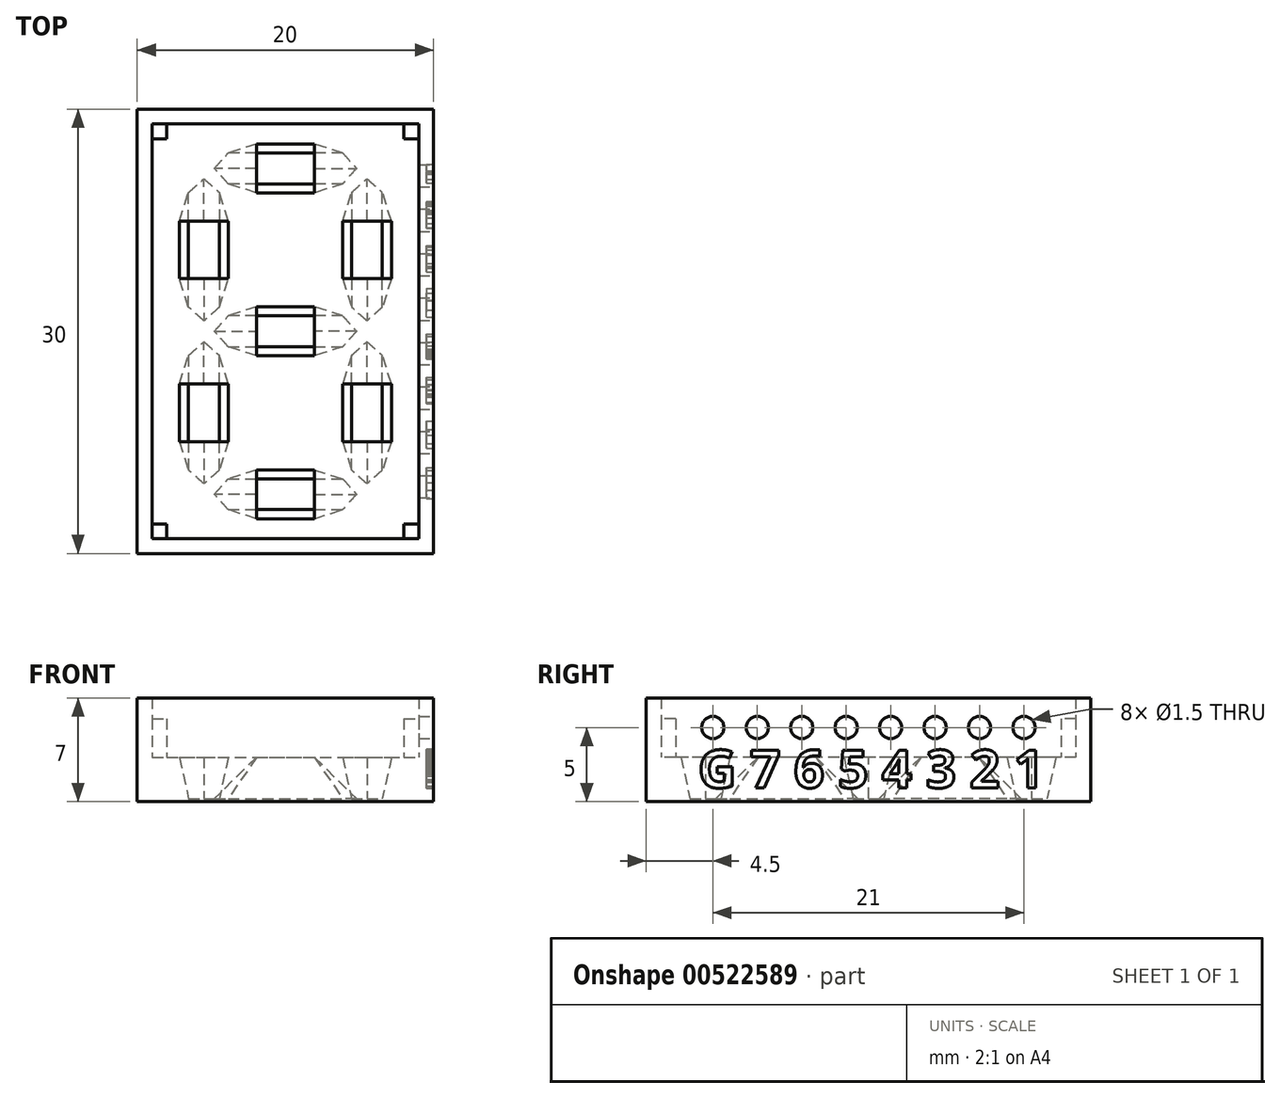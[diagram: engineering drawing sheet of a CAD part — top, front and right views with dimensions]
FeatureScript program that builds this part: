
annotation { "Feature Type Name" : "Feature", "Feature Type Description" : "" }
export const myFeature = defineFeature(function(context is Context, id is Id, definition is map)
    precondition{}
    {
        {
            var Q0;
            Q0=qCreatedBy(makeId("Top.planeOp"),FACE);
            cPlane(context, id + "F0", {"entities" : qUnion([Q0]), "cplaneType" : CPlaneType.OFFSET, "offset" : 3 * mm, "width" : 150 * mm, "height" : 150 * mm});
        }
        {
            var Q0;
            Q0=qCreatedBy(makeId("Top.planeOp"),FACE);
            var sketch = newSketch(context, id + "F1", { "sketchPlane" : qUnion([Q0])});
            skLineSegment(sketch, "E0.bottom", {"start": v(10, -15) * mm, "end": v(-10, -15) * mm});
            skLineSegment(sketch, "E0.top", {"start": v(10, 15) * mm, "end": v(-10, 15) * mm});
            skLineSegment(sketch, "E0.left", {"start": v(10, -15) * mm, "end": v(10, 15) * mm});
            skLineSegment(sketch, "E0.right", {"start": v(-10, -15) * mm, "end": v(-10, 15) * mm});
            skPoint(sketch, "E0.middle", {"position": v(0, 0) * mm});
            skLineSegment(sketch, "E1.bottom", {"start": v(4, -12) * mm, "end": v(-4, -12) * mm});
            skLineSegment(sketch, "E1.top", {"start": v(4, -10) * mm, "end": v(-4, -10) * mm});
            skPoint(sketch, "E1.middle", {"position": v(0, -11) * mm});
            skPoint(sketch, "E2", {"position": v(-5, -11) * mm});
            skPoint(sketch, "E3", {"position": v(5, -11) * mm});
            skPoint(sketch, "E4", {"position": v(4, -10) * mm});
            skPoint(sketch, "E5", {"position": v(-4, -10) * mm});
            skPoint(sketch, "E6", {"position": v(-4, -12) * mm});
            skPoint(sketch, "E7", {"position": v(4, -12) * mm});
            skLineSegment(sketch, "E8", {"start": v(-5, -11) * mm, "end": v(-4, -10) * mm});
            skLineSegment(sketch, "E9", {"start": v(-5, -11) * mm, "end": v(-4, -12) * mm});
            skLineSegment(sketch, "E10", {"start": v(4, -10) * mm, "end": v(5, -11) * mm});
            skLineSegment(sketch, "E11", {"start": v(4, -12) * mm, "end": v(5, -11) * mm});
            skLineSegment(sketch, "E12.bottom", {"start": v(4, -1) * mm, "end": v(-4, -1) * mm});
            skLineSegment(sketch, "E12.top", {"start": v(4, 1) * mm, "end": v(-4, 1) * mm});
            skPoint(sketch, "E13", {"position": v(-5, 0) * mm});
            skPoint(sketch, "E14", {"position": v(5, 0) * mm});
            skPoint(sketch, "E15", {"position": v(4, 1) * mm});
            skPoint(sketch, "E16", {"position": v(-4, 1) * mm});
            skPoint(sketch, "E17", {"position": v(-4, -1) * mm});
            skPoint(sketch, "E18", {"position": v(4, -1) * mm});
            skLineSegment(sketch, "E19", {"start": v(-5, 0) * mm, "end": v(-4, 1) * mm});
            skLineSegment(sketch, "E20", {"start": v(-5, 0) * mm, "end": v(-4, -1) * mm});
            skLineSegment(sketch, "E21", {"start": v(4, 1) * mm, "end": v(5, 0) * mm});
            skLineSegment(sketch, "E22", {"start": v(4, -1) * mm, "end": v(5, 0) * mm});
            skLineSegment(sketch, "E23.bottom", {"start": v(4, 10) * mm, "end": v(-4, 10) * mm});
            skLineSegment(sketch, "E23.top", {"start": v(4, 12) * mm, "end": v(-4, 12) * mm});
            skPoint(sketch, "E23.middle", {"position": v(0, 11) * mm});
            skPoint(sketch, "E24", {"position": v(-5, 11) * mm});
            skPoint(sketch, "E25", {"position": v(5, 11) * mm});
            skPoint(sketch, "E26", {"position": v(4, 12) * mm});
            skPoint(sketch, "E27", {"position": v(-4, 12) * mm});
            skPoint(sketch, "E28", {"position": v(-4, 10) * mm});
            skPoint(sketch, "E29", {"position": v(4, 10) * mm});
            skLineSegment(sketch, "E30", {"start": v(-5, 11) * mm, "end": v(-4, 12) * mm});
            skLineSegment(sketch, "E31", {"start": v(-5, 11) * mm, "end": v(-4, 10) * mm});
            skLineSegment(sketch, "E32", {"start": v(4, 12) * mm, "end": v(5, 11) * mm});
            skLineSegment(sketch, "E33", {"start": v(4, 10) * mm, "end": v(5, 11) * mm});
            skLineSegment(sketch, "E34.bottom", {"start": v(4.5, 1.5) * mm, "end": v(4.5, 9.5) * mm});
            skLineSegment(sketch, "E34.top", {"start": v(6.5, 1.5) * mm, "end": v(6.5, 9.5) * mm});
            skPoint(sketch, "E34.middle", {"position": v(5.5, 5.5) * mm});
            skPoint(sketch, "E35", {"position": v(5.5, 10.5) * mm});
            skPoint(sketch, "E36", {"position": v(5.5, 0.5) * mm});
            skPoint(sketch, "E37", {"position": v(6.5, 1.5) * mm});
            skPoint(sketch, "E38", {"position": v(6.5, 9.5) * mm});
            skPoint(sketch, "E39", {"position": v(4.5, 9.5) * mm});
            skPoint(sketch, "E40", {"position": v(4.5, 1.5) * mm});
            skLineSegment(sketch, "E41", {"start": v(5.5, 10.5) * mm, "end": v(6.5, 9.5) * mm});
            skLineSegment(sketch, "E42", {"start": v(5.5, 10.5) * mm, "end": v(4.5, 9.5) * mm});
            skLineSegment(sketch, "E43", {"start": v(6.5, 1.5) * mm, "end": v(5.5, 0.5) * mm});
            skLineSegment(sketch, "E44", {"start": v(4.5, 1.5) * mm, "end": v(5.5, 0.5) * mm});
            skLineSegment(sketch, "E45.bottom", {"start": v(4.5, -9.5) * mm, "end": v(4.5, -1.5) * mm});
            skLineSegment(sketch, "E45.top", {"start": v(6.5, -9.5) * mm, "end": v(6.5, -1.5) * mm});
            skPoint(sketch, "E45.middle", {"position": v(5.5, -5.5) * mm});
            skPoint(sketch, "E46", {"position": v(5.5, -0.5) * mm});
            skPoint(sketch, "E47", {"position": v(5.5, -10.5) * mm});
            skPoint(sketch, "E48", {"position": v(6.5, -9.5) * mm});
            skPoint(sketch, "E49", {"position": v(6.5, -1.5) * mm});
            skPoint(sketch, "E50", {"position": v(4.5, -1.5) * mm});
            skPoint(sketch, "E51", {"position": v(4.5, -9.5) * mm});
            skLineSegment(sketch, "E52", {"start": v(5.5, -0.5) * mm, "end": v(6.5, -1.5) * mm});
            skLineSegment(sketch, "E53", {"start": v(5.5, -0.5) * mm, "end": v(4.5, -1.5) * mm});
            skLineSegment(sketch, "E54", {"start": v(6.5, -9.5) * mm, "end": v(5.5, -10.5) * mm});
            skLineSegment(sketch, "E55", {"start": v(4.5, -9.5) * mm, "end": v(5.5, -10.5) * mm});
            skLineSegment(sketch, "E56.bottom", {"start": v(-6.5, 1.5) * mm, "end": v(-6.5, 9.5) * mm});
            skLineSegment(sketch, "E56.top", {"start": v(-4.5, 1.5) * mm, "end": v(-4.5, 9.5) * mm});
            skPoint(sketch, "E56.middle", {"position": v(-5.5, 5.5) * mm});
            skPoint(sketch, "E57", {"position": v(-5.5, 10.5) * mm});
            skPoint(sketch, "E58", {"position": v(-5.5, 0.5) * mm});
            skPoint(sketch, "E59", {"position": v(-4.5, 1.5) * mm});
            skPoint(sketch, "E60", {"position": v(-4.5, 9.5) * mm});
            skPoint(sketch, "E61", {"position": v(-6.5, 9.5) * mm});
            skPoint(sketch, "E62", {"position": v(-6.5, 1.5) * mm});
            skLineSegment(sketch, "E63", {"start": v(-5.5, 10.5) * mm, "end": v(-4.5, 9.5) * mm});
            skLineSegment(sketch, "E64", {"start": v(-5.5, 10.5) * mm, "end": v(-6.5, 9.5) * mm});
            skLineSegment(sketch, "E65", {"start": v(-4.5, 1.5) * mm, "end": v(-5.5, 0.5) * mm});
            skLineSegment(sketch, "E66", {"start": v(-6.5, 1.5) * mm, "end": v(-5.5, 0.5) * mm});
            skLineSegment(sketch, "E67.bottom", {"start": v(-6.5, -9.5) * mm, "end": v(-6.5, -1.5) * mm});
            skLineSegment(sketch, "E67.top", {"start": v(-4.5, -9.5) * mm, "end": v(-4.5, -1.5) * mm});
            skPoint(sketch, "E67.middle", {"position": v(-5.5, -5.5) * mm});
            skPoint(sketch, "E68", {"position": v(-5.5, -0.5) * mm});
            skPoint(sketch, "E69", {"position": v(-5.5, -10.5) * mm});
            skPoint(sketch, "E70", {"position": v(-4.5, -9.5) * mm});
            skPoint(sketch, "E71", {"position": v(-4.5, -1.5) * mm});
            skPoint(sketch, "E72", {"position": v(-6.5, -1.5) * mm});
            skPoint(sketch, "E73", {"position": v(-6.5, -9.5) * mm});
            skLineSegment(sketch, "E74", {"start": v(-5.5, -0.5) * mm, "end": v(-4.5, -1.5) * mm});
            skLineSegment(sketch, "E75", {"start": v(-5.5, -0.5) * mm, "end": v(-6.5, -1.5) * mm});
            skLineSegment(sketch, "E76", {"start": v(-4.5, -9.5) * mm, "end": v(-5.5, -10.5) * mm});
            skLineSegment(sketch, "E77", {"start": v(-6.5, -9.5) * mm, "end": v(-5.5, -10.5) * mm});
            skLineSegment(sketch, "E78", {"start": v(0, 0) * mm, "end": v(0, 11) * mm, "construction": true});
            skLineSegment(sketch, "E79", {"start": v(0, 0) * mm, "end": v(0, -11) * mm, "construction": true});
            skLineSegment(sketch, "E80", {"start": v(0, 5.5) * mm, "end": v(5.5, 5.5) * mm, "construction": true});
            skLineSegment(sketch, "E81", {"start": v(5.5, 0) * mm, "end": v(5.5, -5.5) * mm, "construction": true});
            skLineSegment(sketch, "E82", {"start": v(0, -5.5) * mm, "end": v(-5.5, -5.5) * mm, "construction": true});
            skLineSegment(sketch, "E83", {"start": v(0, -5.5) * mm, "end": v(5.5, -5.5) * mm, "construction": true});
            skLineSegment(sketch, "E84", {"start": v(5.5, 0) * mm, "end": v(5.5, 5.5) * mm, "construction": true});
            skLineSegment(sketch, "E85", {"start": v(0, 5.5) * mm, "end": v(-5.5, 5.5) * mm, "construction": true});
            skLineSegment(sketch, "E86.0", {"start": v(9, 14) * mm, "end": v(-9, 14) * mm});
            skLineSegment(sketch, "E86.1", {"start": v(9, -14) * mm, "end": v(9, 14) * mm});
            skLineSegment(sketch, "E86.2", {"start": v(9, -14) * mm, "end": v(-9, -14) * mm});
            skLineSegment(sketch, "E86.3", {"start": v(-9, -14) * mm, "end": v(-9, 14) * mm});
            skSolve(sketch);
        }
        {
            var Q0;
            Q0=qCreatedBy(id+"F0.planeOp",FACE);
            var sketch = newSketch(context, id + "F2", { "sketchPlane" : qUnion([Q0])});
            skPoint(sketch, "E87.1", {"position": v(5.5, 5.5) * mm});
            skPoint(sketch, "E87.2", {"position": v(-5.5, 5.5) * mm});
            skPoint(sketch, "E87.3", {"position": v(-5.5, -5.5) * mm});
            skPoint(sketch, "E87.5", {"position": v(5.5, -5.5) * mm});
            skLineSegment(sketch, "E88.bottom", {"start": v(1.95, -1.65) * mm, "end": v(-1.95, -1.65) * mm});
            skLineSegment(sketch, "E88.top", {"start": v(1.95, 1.65) * mm, "end": v(-1.95, 1.65) * mm});
            skLineSegment(sketch, "E88.left", {"start": v(1.95, -1.65) * mm, "end": v(1.95, 1.65) * mm});
            skLineSegment(sketch, "E88.right", {"start": v(-1.95, -1.65) * mm, "end": v(-1.95, 1.65) * mm});
            skPoint(sketch, "E88.middle", {"position": v(0, 0) * mm});
            skLineSegment(sketch, "E89.bottom", {"start": v(7.15, 3.55) * mm, "end": v(3.85, 3.55) * mm});
            skLineSegment(sketch, "E89.top", {"start": v(7.15, 7.45) * mm, "end": v(3.85, 7.45) * mm});
            skLineSegment(sketch, "E89.left", {"start": v(7.15, 3.55) * mm, "end": v(7.15, 7.45) * mm});
            skLineSegment(sketch, "E89.right", {"start": v(3.85, 3.55) * mm, "end": v(3.85, 7.45) * mm});
            skLineSegment(sketch, "E90.bottom", {"start": v(7.15, -7.45) * mm, "end": v(3.85, -7.45) * mm});
            skLineSegment(sketch, "E90.top", {"start": v(7.15, -3.55) * mm, "end": v(3.85, -3.55) * mm});
            skLineSegment(sketch, "E90.left", {"start": v(7.15, -7.45) * mm, "end": v(7.15, -3.55) * mm});
            skLineSegment(sketch, "E90.right", {"start": v(3.85, -7.45) * mm, "end": v(3.85, -3.55) * mm});
            skLineSegment(sketch, "E91.bottom", {"start": v(-3.85, -7.45) * mm, "end": v(-7.15, -7.45) * mm});
            skLineSegment(sketch, "E91.top", {"start": v(-3.85, -3.55) * mm, "end": v(-7.15, -3.55) * mm});
            skLineSegment(sketch, "E91.left", {"start": v(-3.85, -7.45) * mm, "end": v(-3.85, -3.55) * mm});
            skLineSegment(sketch, "E91.right", {"start": v(-7.15, -7.45) * mm, "end": v(-7.15, -3.55) * mm});
            skLineSegment(sketch, "E92.bottom", {"start": v(-3.85, 3.55) * mm, "end": v(-7.15, 3.55) * mm});
            skLineSegment(sketch, "E92.top", {"start": v(-3.85, 7.45) * mm, "end": v(-7.15, 7.45) * mm});
            skLineSegment(sketch, "E92.left", {"start": v(-3.85, 3.55) * mm, "end": v(-3.85, 7.45) * mm});
            skLineSegment(sketch, "E92.right", {"start": v(-7.15, 3.55) * mm, "end": v(-7.15, 7.45) * mm});
            skPoint(sketch, "E93.0", {"position": v(0, -11) * mm});
            skLineSegment(sketch, "E94.bottom", {"start": v(1.95, -12.65) * mm, "end": v(-1.95, -12.65) * mm});
            skLineSegment(sketch, "E94.top", {"start": v(1.95, -9.35) * mm, "end": v(-1.95, -9.35) * mm});
            skLineSegment(sketch, "E94.left", {"start": v(1.95, -12.65) * mm, "end": v(1.95, -9.35) * mm});
            skLineSegment(sketch, "E94.right", {"start": v(-1.95, -12.65) * mm, "end": v(-1.95, -9.35) * mm});
            skPoint(sketch, "E95.0", {"position": v(0, 11) * mm});
            skLineSegment(sketch, "E96.bottom", {"start": v(1.95, 9.35) * mm, "end": v(-1.95, 9.35) * mm});
            skLineSegment(sketch, "E96.top", {"start": v(1.95, 12.65) * mm, "end": v(-1.95, 12.65) * mm});
            skLineSegment(sketch, "E96.left", {"start": v(1.95, 9.35) * mm, "end": v(1.95, 12.65) * mm});
            skLineSegment(sketch, "E96.right", {"start": v(-1.95, 9.35) * mm, "end": v(-1.95, 12.65) * mm});
            skLineSegment(sketch, "E97.0", {"start": v(-9, -14) * mm, "end": v(-9, 14) * mm});
            skLineSegment(sketch, "E97.1", {"start": v(9, 14) * mm, "end": v(-9, 14) * mm});
            skLineSegment(sketch, "E97.2", {"start": v(9, -14) * mm, "end": v(9, 14) * mm});
            skLineSegment(sketch, "E97.3", {"start": v(9, -14) * mm, "end": v(-9, -14) * mm});
            skPoint(sketch, "E98", {"position": v(1.95, 0) * mm});
            skPoint(sketch, "E99", {"position": v(-1.95, 0) * mm});
            skSolve(sketch);
        }
        {
            var Q0;
            Q0=makeQuery(id+"F1.imprint","IMPRINT",FACE,{"disambiguationData":[TD([[makeQuery(id+"F1.imprint","IMPRINT",EDGE,{"derivedFrom":sQuery(id+"F1.wireOp",EDGE,"E56.bottom")}),-1.0]])]});
            var Q1;
            Q1=makeQuery(id+"F1.imprint","IMPRINT",FACE,{"disambiguationData":[TD([[makeQuery(id+"F1.imprint","IMPRINT",EDGE,{"derivedFrom":sQuery(id+"F1.wireOp",EDGE,"E23.bottom")}),-1.0]])]});
            var Q2;
            Q2=makeQuery(id+"F1.imprint","IMPRINT",FACE,{"disambiguationData":[TD([[makeQuery(id+"F1.imprint","IMPRINT",EDGE,{"derivedFrom":sQuery(id+"F1.wireOp",EDGE,"E34.bottom")}),-1.0]])]});
            var Q3;
            Q3=makeQuery(id+"F1.imprint","IMPRINT",FACE,{"disambiguationData":[TD([[makeQuery(id+"F1.imprint","IMPRINT",EDGE,{"derivedFrom":sQuery(id+"F1.wireOp",EDGE,"E12.bottom")}),-1.0]])]});
            var Q4;
            Q4=makeQuery(id+"F1.imprint","IMPRINT",FACE,{"disambiguationData":[TD([[makeQuery(id+"F1.imprint","IMPRINT",EDGE,{"derivedFrom":sQuery(id+"F1.wireOp",EDGE,"E67.bottom")}),-1.0]])]});
            var Q5;
            Q5=makeQuery(id+"F1.imprint","IMPRINT",FACE,{"disambiguationData":[TD([[makeQuery(id+"F1.imprint","IMPRINT",EDGE,{"derivedFrom":sQuery(id+"F1.wireOp",EDGE,"E1.bottom")}),-1.0]])]});
            var Q6;
            Q6=makeQuery(id+"F1.imprint","IMPRINT",FACE,{"disambiguationData":[TD([[makeQuery(id+"F1.imprint","IMPRINT",EDGE,{"derivedFrom":sQuery(id+"F1.wireOp",EDGE,"E45.bottom")}),-1.0]])]});
            var Q7;
            Q7=makeQuery(id+"F1.imprint","IMPRINT",FACE,{"disambiguationData":[TD([[makeQuery(id+"F1.imprint","IMPRINT",EDGE,{"derivedFrom":sQuery(id+"F1.wireOp",EDGE,"E1.bottom")}),1.0]])]});
            extrude(context, id + "F3", {"entities" : qUnion([Q0, Q1, Q2, Q3, Q4, Q5, Q6, Q7]), "depth" : 3 * mm, "offsetDistance" : 25 * mm});
        }
        {
            var Q0;
            Q0=sQuery(id+"F2.wireOp",VERTEX,"E96.top.start");
            var Q1;
            Q1=sQuery(id+"F2.wireOp",VERTEX,"E96.top.end");
            var Q2;
            Q2=sQuery(id+"F1.wireOp",VERTEX,"E27");
            cPlane(context, id + "F4", {"entities" : qUnion([Q0, Q1, Q2]), "cplaneType" : CPlaneType.THREE_POINT, "offset" : 25 * mm, "width" : 150 * mm, "height" : 150 * mm});
        }
        {
            var Q0;
            Q0=sQuery(id+"F2.wireOp",VERTEX,"E96.left.start");
            var Q1;
            Q1=sQuery(id+"F2.wireOp",VERTEX,"E96.bottom.end");
            var Q2;
            Q2=sQuery(id+"F1.wireOp",VERTEX,"E28");
            cPlane(context, id + "F5", {"entities" : qUnion([Q0, Q1, Q2]), "cplaneType" : CPlaneType.THREE_POINT, "offset" : 25 * mm, "width" : 150 * mm, "height" : 150 * mm});
        }
        {
            var Q0;
            Q0=qCreatedBy(id+"F4.planeOp",FACE);
            var sketch = newSketch(context, id + "F6", { "sketchPlane" : qUnion([Q0])});
            skPoint(sketch, "E100.0", {"position": v(1.95, 5.61) * mm});
            skPoint(sketch, "E100.1", {"position": v(4, 2.54) * mm});
            skPoint(sketch, "E100.2", {"position": v(-4, 2.54) * mm});
            skPoint(sketch, "E100.3", {"position": v(-1.95, 5.61) * mm});
            skLineSegment(sketch, "E101", {"start": v(1.95, 5.61) * mm, "end": v(4, 2.54) * mm});
            skLineSegment(sketch, "E102", {"start": v(-1.95, 5.61) * mm, "end": v(-4, 2.54) * mm});
            skSolve(sketch);
        }
        {
            var Q0;
            Q0=qCreatedBy(id+"F5.planeOp",FACE);
            var sketch = newSketch(context, id + "F7", { "sketchPlane" : qUnion([Q0])});
            skPoint(sketch, "E103.0", {"position": v(-1.95, 0.95) * mm});
            skPoint(sketch, "E103.1", {"position": v(-4, -2.12) * mm});
            skPoint(sketch, "E103.2", {"position": v(1.95, 0.95) * mm});
            skPoint(sketch, "E103.3", {"position": v(4, -2.12) * mm});
            skLineSegment(sketch, "E104", {"start": v(1.95, 0.95) * mm, "end": v(4, -2.12) * mm});
            skLineSegment(sketch, "E105", {"start": v(-1.95, 0.95) * mm, "end": v(-4, -2.12) * mm});
            skSolve(sketch);
        }
        {
            var Q1;
            Q1=makeQuery(id+"F2.imprint","IMPRINT",FACE,{"disambiguationData":[TD([[makeQuery(id+"F2.imprint","IMPRINT",EDGE,{"derivedFrom":sQuery(id+"F2.wireOp",EDGE,"E96.bottom")}),-1.0]])]});
            var Q2;
            Q2=makeQuery(id+"F1.imprint","IMPRINT",FACE,{"disambiguationData":[TD([[makeQuery(id+"F1.imprint","IMPRINT",EDGE,{"derivedFrom":sQuery(id+"F1.wireOp",EDGE,"E23.bottom")}),-1.0]])]});
            var Q3;
            Q3=sQuery(id+"F6.wireOp",EDGE,"E101");
            var Q4;
            Q4=sQuery(id+"F7.wireOp",EDGE,"E104");
            var Q5;
            Q5=sQuery(id+"F6.wireOp",EDGE,"E102");
            var Q6;
            Q6=sQuery(id+"F7.wireOp",EDGE,"E105");
            loft(context, id + "F8", {"operationType" : NewBodyOperationType.REMOVE, "addGuides" : true, "sheetProfilesArray" : [{ "sheetProfileEntities" : qUnion([Q1]) }, { "sheetProfileEntities" : qUnion([Q2]) }], "guidesArray" : [{ "guideEntities" : qUnion([Q3]), "guideDerivativeType" : LoftGuideDerivativeType.DEFAULT, "guideDerivativeMagnitude" : 1 }, { "guideEntities" : qUnion([Q4]), "guideDerivativeType" : LoftGuideDerivativeType.DEFAULT, "guideDerivativeMagnitude" : 1 }, { "guideEntities" : qUnion([Q5]), "guideDerivativeType" : LoftGuideDerivativeType.DEFAULT, "guideDerivativeMagnitude" : 1 }, { "guideEntities" : qUnion([Q6]), "guideDerivativeType" : LoftGuideDerivativeType.DEFAULT, "guideDerivativeMagnitude" : 1 }]});
        }
        {
            var Q0;
            Q0=sQuery(id+"F1.wireOp",VERTEX,"E16");
            var Q1;
            Q1=sQuery(id+"F2.wireOp",VERTEX,"E88.right.end");
            var Q2;
            Q2=sQuery(id+"F2.wireOp",VERTEX,"E88.left.end");
            cPlane(context, id + "F9", {"entities" : qUnion([Q0, Q1, Q2]), "cplaneType" : CPlaneType.THREE_POINT, "offset" : 25 * mm, "width" : 150 * mm, "height" : 150 * mm});
        }
        {
            var Q0;
            Q0=sQuery(id+"F2.wireOp",VERTEX,"E88.right.start");
            var Q1;
            Q1=sQuery(id+"F1.wireOp",VERTEX,"E17");
            var Q2;
            Q2=sQuery(id+"F2.wireOp",VERTEX,"E88.left.start");
            cPlane(context, id + "F10", {"entities" : qUnion([Q0, Q1, Q2]), "cplaneType" : CPlaneType.THREE_POINT, "offset" : 25 * mm, "width" : 150 * mm, "height" : 150 * mm});
        }
        {
            var Q0;
            Q0=qCreatedBy(id+"F9.planeOp",FACE);
            var sketch = newSketch(context, id + "F11", { "sketchPlane" : qUnion([Q0])});
            skPoint(sketch, "E106.0", {"position": v(-4, 0.21) * mm});
            skPoint(sketch, "E106.1", {"position": v(-1.95, 3.28) * mm});
            skPoint(sketch, "E106.2", {"position": v(1.95, 3.28) * mm});
            skPoint(sketch, "E106.3", {"position": v(4, 0.21) * mm});
            skLineSegment(sketch, "E107", {"start": v(-4, 0.21) * mm, "end": v(-1.95, 3.28) * mm});
            skLineSegment(sketch, "E108", {"start": v(1.95, 3.28) * mm, "end": v(4, 0.21) * mm});
            skSolve(sketch);
        }
        {
            var Q0;
            Q0=qCreatedBy(id+"F10.planeOp",FACE);
            var sketch = newSketch(context, id + "F12", { "sketchPlane" : qUnion([Q0])});
            skPoint(sketch, "E109.0", {"position": v(4, 0.21) * mm});
            skPoint(sketch, "E109.1", {"position": v(1.95, 3.28) * mm});
            skPoint(sketch, "E109.2", {"position": v(-1.95, 3.28) * mm});
            skPoint(sketch, "E109.3", {"position": v(-4, 0.21) * mm});
            skLineSegment(sketch, "E110", {"start": v(4, 0.21) * mm, "end": v(1.95, 3.28) * mm});
            skLineSegment(sketch, "E111", {"start": v(-1.95, 3.28) * mm, "end": v(-4, 0.21) * mm});
            skSolve(sketch);
        }
        {
            var Q1;
            Q1=makeQuery(id+"F1.imprint","IMPRINT",FACE,{"disambiguationData":[TD([[makeQuery(id+"F1.imprint","IMPRINT",EDGE,{"derivedFrom":sQuery(id+"F1.wireOp",EDGE,"E12.bottom")}),-1.0]])]});
            var Q2;
            Q2=makeQuery(id+"F2.imprint","IMPRINT",FACE,{"disambiguationData":[TD([[makeQuery(id+"F2.imprint","IMPRINT",EDGE,{"derivedFrom":sQuery(id+"F2.wireOp",EDGE,"E88.bottom")}),-1.0]])]});
            var Q3;
            Q3=sQuery(id+"F12.wireOp",EDGE,"E111");
            var Q4;
            Q4=sQuery(id+"F11.wireOp",EDGE,"E108");
            var Q5;
            Q5=sQuery(id+"F11.wireOp",EDGE,"E107");
            var Q6;
            Q6=sQuery(id+"F12.wireOp",EDGE,"E110");
            loft(context, id + "F13", {"operationType" : NewBodyOperationType.REMOVE, "addGuides" : true, "sheetProfilesArray" : [{ "sheetProfileEntities" : qUnion([Q1]) }, { "sheetProfileEntities" : qUnion([Q2]) }], "guidesArray" : [{ "guideEntities" : qUnion([Q3]), "guideDerivativeType" : LoftGuideDerivativeType.DEFAULT, "guideDerivativeMagnitude" : 1 }, { "guideEntities" : qUnion([Q4]), "guideDerivativeType" : LoftGuideDerivativeType.DEFAULT, "guideDerivativeMagnitude" : 1 }, { "guideEntities" : qUnion([Q5]), "guideDerivativeType" : LoftGuideDerivativeType.DEFAULT, "guideDerivativeMagnitude" : 1 }, { "guideEntities" : qUnion([Q6]), "guideDerivativeType" : LoftGuideDerivativeType.DEFAULT, "guideDerivativeMagnitude" : 1 }]});
        }
        {
            var Q0;
            Q0=sQuery(id+"F2.wireOp",VERTEX,"E94.right.end");
            var Q1;
            Q1=sQuery(id+"F1.wireOp",VERTEX,"E5");
            var Q2;
            Q2=sQuery(id+"F2.wireOp",VERTEX,"E94.left.end");
            cPlane(context, id + "F14", {"entities" : qUnion([Q0, Q1, Q2]), "cplaneType" : CPlaneType.THREE_POINT, "offset" : 25 * mm, "width" : 150 * mm, "height" : 150 * mm});
        }
        {
            var Q0;
            Q0=sQuery(id+"F2.wireOp",VERTEX,"E94.bottom.end");
            var Q1;
            Q1=sQuery(id+"F1.wireOp",VERTEX,"E6");
            var Q2;
            Q2=sQuery(id+"F2.wireOp",VERTEX,"E94.bottom.start");
            cPlane(context, id + "F15", {"entities" : qUnion([Q0, Q1, Q2]), "cplaneType" : CPlaneType.THREE_POINT, "offset" : 25 * mm, "width" : 150 * mm, "height" : 150 * mm});
        }
        {
            var Q0;
            Q0=qCreatedBy(id+"F14.planeOp",FACE);
            var sketch = newSketch(context, id + "F16", { "sketchPlane" : qUnion([Q0])});
            skPoint(sketch, "E112.0", {"position": v(4, -2.12) * mm});
            skPoint(sketch, "E112.1", {"position": v(1.95, 0.95) * mm});
            skPoint(sketch, "E112.2", {"position": v(-1.95, 0.95) * mm});
            skPoint(sketch, "E112.3", {"position": v(-4, -2.12) * mm});
            skLineSegment(sketch, "E113", {"start": v(4, -2.12) * mm, "end": v(1.95, 0.95) * mm});
            skLineSegment(sketch, "E114", {"start": v(-1.95, 0.95) * mm, "end": v(-4, -2.12) * mm});
            skSolve(sketch);
        }
        {
            var Q0;
            Q0=qCreatedBy(id+"F15.planeOp",FACE);
            var sketch = newSketch(context, id + "F17", { "sketchPlane" : qUnion([Q0])});
            skPoint(sketch, "E115.0", {"position": v(-1.95, 5.61) * mm});
            skPoint(sketch, "E115.1", {"position": v(1.95, 5.61) * mm});
            skPoint(sketch, "E115.2", {"position": v(4, 2.54) * mm});
            skPoint(sketch, "E115.3", {"position": v(-4, 2.54) * mm});
            skLineSegment(sketch, "E116", {"start": v(4, 2.54) * mm, "end": v(1.95, 5.61) * mm});
            skLineSegment(sketch, "E117", {"start": v(-1.95, 5.61) * mm, "end": v(-4, 2.54) * mm});
            skSolve(sketch);
        }
        {
            var Q1;
            Q1=makeQuery(id+"F2.imprint","IMPRINT",FACE,{"disambiguationData":[TD([[makeQuery(id+"F2.imprint","IMPRINT",EDGE,{"derivedFrom":sQuery(id+"F2.wireOp",EDGE,"E94.bottom")}),-1.0]])]});
            var Q2;
            Q2=makeQuery(id+"F1.imprint","IMPRINT",FACE,{"disambiguationData":[TD([[makeQuery(id+"F1.imprint","IMPRINT",EDGE,{"derivedFrom":sQuery(id+"F1.wireOp",EDGE,"E1.bottom")}),-1.0]])]});
            var Q3;
            Q3=sQuery(id+"F16.wireOp",EDGE,"E113");
            var Q4;
            Q4=sQuery(id+"F17.wireOp",EDGE,"E116");
            var Q5;
            Q5=sQuery(id+"F17.wireOp",EDGE,"E117");
            var Q6;
            Q6=sQuery(id+"F16.wireOp",EDGE,"E114");
            loft(context, id + "F18", {"operationType" : NewBodyOperationType.REMOVE, "addGuides" : true, "sheetProfilesArray" : [{ "sheetProfileEntities" : qUnion([Q1]) }, { "sheetProfileEntities" : qUnion([Q2]) }], "guidesArray" : [{ "guideEntities" : qUnion([Q3]), "guideDerivativeType" : LoftGuideDerivativeType.DEFAULT, "guideDerivativeMagnitude" : 1 }, { "guideEntities" : qUnion([Q4]), "guideDerivativeType" : LoftGuideDerivativeType.DEFAULT, "guideDerivativeMagnitude" : 1 }, { "guideEntities" : qUnion([Q5]), "guideDerivativeType" : LoftGuideDerivativeType.DEFAULT, "guideDerivativeMagnitude" : 1 }, { "guideEntities" : qUnion([Q6]), "guideDerivativeType" : LoftGuideDerivativeType.DEFAULT, "guideDerivativeMagnitude" : 1 }]});
        }
        {
            var Q0;
            Q0=sQuery(id+"F2.wireOp",VERTEX,"E92.top.end");
            var Q1;
            Q1=sQuery(id+"F2.wireOp",VERTEX,"E92.bottom.end");
            var Q2;
            Q2=sQuery(id+"F1.wireOp",VERTEX,"E62");
            cPlane(context, id + "F19", {"entities" : qUnion([Q0, Q1, Q2]), "cplaneType" : CPlaneType.THREE_POINT, "offset" : 25 * mm, "width" : 150 * mm, "height" : 150 * mm});
        }
        {
            var Q0;
            Q0=sQuery(id+"F2.wireOp",VERTEX,"E92.top.start");
            var Q1;
            Q1=sQuery(id+"F2.wireOp",VERTEX,"E92.left.start");
            var Q2;
            Q2=sQuery(id+"F1.wireOp",VERTEX,"E59");
            cPlane(context, id + "F20", {"entities" : qUnion([Q0, Q1, Q2]), "cplaneType" : CPlaneType.THREE_POINT, "offset" : 25 * mm, "width" : 150 * mm, "height" : 150 * mm});
        }
        {
            var Q0;
            Q0=qCreatedBy(id+"F19.planeOp",FACE);
            var sketch = newSketch(context, id + "F21", { "sketchPlane" : qUnion([Q0])});
            skPoint(sketch, "E118.0", {"position": v(-7.45, 4.45) * mm});
            skPoint(sketch, "E118.1", {"position": v(-3.55, 4.45) * mm});
            skPoint(sketch, "E118.2", {"position": v(-1.5, 1.38) * mm});
            skPoint(sketch, "E118.3", {"position": v(-9.5, 1.38) * mm});
            skPoint(sketch, "E118.4", {"position": v(1.5, 1.38) * mm});
            skPoint(sketch, "E118.5", {"position": v(3.55, 4.45) * mm});
            skPoint(sketch, "E118.6", {"position": v(7.45, 4.45) * mm});
            skPoint(sketch, "E118.7", {"position": v(9.5, 1.38) * mm});
            skLineSegment(sketch, "E119", {"start": v(7.45, 4.45) * mm, "end": v(9.5, 1.38) * mm});
            skLineSegment(sketch, "E120", {"start": v(3.55, 4.45) * mm, "end": v(1.5, 1.38) * mm});
            skLineSegment(sketch, "E121", {"start": v(-3.55, 4.45) * mm, "end": v(-1.5, 1.38) * mm});
            skLineSegment(sketch, "E122", {"start": v(-7.45, 4.45) * mm, "end": v(-9.5, 1.38) * mm});
            skSolve(sketch);
        }
        {
            var Q0;
            Q0=qCreatedBy(id+"F20.planeOp",FACE);
            var sketch = newSketch(context, id + "F22", { "sketchPlane" : qUnion([Q0])});
            skPoint(sketch, "E123.0", {"position": v(-7.45, 2.12) * mm});
            skPoint(sketch, "E123.1", {"position": v(-9.5, -0.95) * mm});
            skPoint(sketch, "E123.2", {"position": v(-3.55, 2.12) * mm});
            skPoint(sketch, "E123.3", {"position": v(-1.5, -0.95) * mm});
            skPoint(sketch, "E123.4", {"position": v(1.5, -0.95) * mm});
            skPoint(sketch, "E123.5", {"position": v(3.55, 2.12) * mm});
            skPoint(sketch, "E123.6", {"position": v(7.45, 2.12) * mm});
            skPoint(sketch, "E123.7", {"position": v(9.5, -0.95) * mm});
            skLineSegment(sketch, "E124", {"start": v(7.45, 2.12) * mm, "end": v(9.5, -0.95) * mm});
            skLineSegment(sketch, "E125", {"start": v(3.55, 2.12) * mm, "end": v(1.5, -0.95) * mm});
            skLineSegment(sketch, "E126", {"start": v(-1.5, -0.95) * mm, "end": v(-3.55, 2.12) * mm});
            skLineSegment(sketch, "E127", {"start": v(-7.45, 2.12) * mm, "end": v(-9.5, -0.95) * mm});
            skSolve(sketch);
        }
        {
            var Q1;
            Q1=makeQuery(id+"F2.imprint","IMPRINT",FACE,{"disambiguationData":[TD([[makeQuery(id+"F2.imprint","IMPRINT",EDGE,{"derivedFrom":sQuery(id+"F2.wireOp",EDGE,"E91.bottom")}),-1.0]])]});
            var Q2;
            Q2=makeQuery(id+"F1.imprint","IMPRINT",FACE,{"disambiguationData":[TD([[makeQuery(id+"F1.imprint","IMPRINT",EDGE,{"derivedFrom":sQuery(id+"F1.wireOp",EDGE,"E67.bottom")}),-1.0]])]});
            var Q3;
            Q3=sQuery(id+"F21.wireOp",EDGE,"E120");
            var Q4;
            Q4=sQuery(id+"F21.wireOp",EDGE,"E119");
            var Q5;
            Q5=sQuery(id+"F22.wireOp",EDGE,"E124");
            var Q6;
            Q6=sQuery(id+"F22.wireOp",EDGE,"E125");
            loft(context, id + "F23", {"operationType" : NewBodyOperationType.REMOVE, "addGuides" : true, "sheetProfilesArray" : [{ "sheetProfileEntities" : qUnion([Q1]) }, { "sheetProfileEntities" : qUnion([Q2]) }], "guidesArray" : [{ "guideEntities" : qUnion([Q3]), "guideDerivativeType" : LoftGuideDerivativeType.DEFAULT, "guideDerivativeMagnitude" : 1 }, { "guideEntities" : qUnion([Q4]), "guideDerivativeType" : LoftGuideDerivativeType.DEFAULT, "guideDerivativeMagnitude" : 1 }, { "guideEntities" : qUnion([Q5]), "guideDerivativeType" : LoftGuideDerivativeType.DEFAULT, "guideDerivativeMagnitude" : 1 }, { "guideEntities" : qUnion([Q6]), "guideDerivativeType" : LoftGuideDerivativeType.DEFAULT, "guideDerivativeMagnitude" : 1 }]});
        }
        {
            var Q1;
            Q1=makeQuery(id+"F2.imprint","IMPRINT",FACE,{"disambiguationData":[TD([[makeQuery(id+"F2.imprint","IMPRINT",EDGE,{"derivedFrom":sQuery(id+"F2.wireOp",EDGE,"E92.bottom")}),-1.0]])]});
            var Q2;
            Q2=makeQuery(id+"F1.imprint","IMPRINT",FACE,{"disambiguationData":[TD([[makeQuery(id+"F1.imprint","IMPRINT",EDGE,{"derivedFrom":sQuery(id+"F1.wireOp",EDGE,"E56.bottom")}),-1.0]])]});
            var Q3;
            Q3=sQuery(id+"F21.wireOp",EDGE,"E121");
            var Q4;
            Q4=sQuery(id+"F21.wireOp",EDGE,"E122");
            var Q5;
            Q5=sQuery(id+"F22.wireOp",EDGE,"E127");
            var Q6;
            Q6=sQuery(id+"F22.wireOp",EDGE,"E126");
            loft(context, id + "F24", {"operationType" : NewBodyOperationType.REMOVE, "addGuides" : true, "sheetProfilesArray" : [{ "sheetProfileEntities" : qUnion([Q1]) }, { "sheetProfileEntities" : qUnion([Q2]) }], "guidesArray" : [{ "guideEntities" : qUnion([Q3]), "guideDerivativeType" : LoftGuideDerivativeType.DEFAULT, "guideDerivativeMagnitude" : 1 }, { "guideEntities" : qUnion([Q4]), "guideDerivativeType" : LoftGuideDerivativeType.DEFAULT, "guideDerivativeMagnitude" : 1 }, { "guideEntities" : qUnion([Q5]), "guideDerivativeType" : LoftGuideDerivativeType.DEFAULT, "guideDerivativeMagnitude" : 1 }, { "guideEntities" : qUnion([Q6]), "guideDerivativeType" : LoftGuideDerivativeType.DEFAULT, "guideDerivativeMagnitude" : 1 }]});
        }
        {
            var Q0;
            Q0=sQuery(id+"F2.wireOp",VERTEX,"E90.left.start");
            var Q1;
            Q1=sQuery(id+"F2.wireOp",VERTEX,"E90.left.end");
            var Q2;
            Q2=sQuery(id+"F1.wireOp",VERTEX,"E48");
            cPlane(context, id + "F25", {"entities" : qUnion([Q0, Q1, Q2]), "cplaneType" : CPlaneType.THREE_POINT, "offset" : 25 * mm, "width" : 150 * mm, "height" : 150 * mm});
        }
        {
            var Q0;
            Q0=sQuery(id+"F1.wireOp",VERTEX,"E51");
            var Q1;
            Q1=sQuery(id+"F2.wireOp",VERTEX,"E90.right.start");
            var Q2;
            Q2=sQuery(id+"F2.wireOp",VERTEX,"E90.right.end");
            cPlane(context, id + "F26", {"entities" : qUnion([Q0, Q1, Q2]), "cplaneType" : CPlaneType.THREE_POINT, "offset" : 25 * mm, "width" : 150 * mm, "height" : 150 * mm});
        }
        {
            var Q0;
            Q0=qCreatedBy(id+"F25.planeOp",FACE);
            var sketch = newSketch(context, id + "F27", { "sketchPlane" : qUnion([Q0])});
            skPoint(sketch, "E128.0", {"position": v(-9.5, 1.38) * mm});
            skPoint(sketch, "E128.1", {"position": v(-7.45, 4.45) * mm});
            skPoint(sketch, "E128.2", {"position": v(-3.55, 4.45) * mm});
            skPoint(sketch, "E128.3", {"position": v(-1.5, 1.38) * mm});
            skPoint(sketch, "E128.4", {"position": v(1.5, 1.38) * mm});
            skPoint(sketch, "E128.5", {"position": v(3.55, 4.45) * mm});
            skPoint(sketch, "E128.6", {"position": v(7.45, 4.45) * mm});
            skPoint(sketch, "E128.7", {"position": v(9.5, 1.38) * mm});
            skLineSegment(sketch, "E129", {"start": v(7.45, 4.45) * mm, "end": v(9.5, 1.38) * mm});
            skLineSegment(sketch, "E130", {"start": v(3.55, 4.45) * mm, "end": v(1.5, 1.38) * mm});
            skLineSegment(sketch, "E131", {"start": v(-1.5, 1.38) * mm, "end": v(-3.55, 4.45) * mm});
            skLineSegment(sketch, "E132", {"start": v(-7.45, 4.45) * mm, "end": v(-9.5, 1.38) * mm});
            skSolve(sketch);
        }
        {
            var Q0;
            Q0=qCreatedBy(id+"F26.planeOp",FACE);
            var sketch = newSketch(context, id + "F28", { "sketchPlane" : qUnion([Q0])});
            skPoint(sketch, "E133.0", {"position": v(-9.5, -0.95) * mm});
            skPoint(sketch, "E133.1", {"position": v(-7.45, 2.12) * mm});
            skPoint(sketch, "E133.2", {"position": v(-3.55, 2.12) * mm});
            skPoint(sketch, "E133.3", {"position": v(-1.5, -0.95) * mm});
            skPoint(sketch, "E133.4", {"position": v(1.5, -0.95) * mm});
            skPoint(sketch, "E133.5", {"position": v(3.55, 2.12) * mm});
            skPoint(sketch, "E133.6", {"position": v(7.45, 2.12) * mm});
            skPoint(sketch, "E133.7", {"position": v(9.5, -0.95) * mm});
            skLineSegment(sketch, "E134", {"start": v(7.45, 2.12) * mm, "end": v(9.5, -0.95) * mm});
            skLineSegment(sketch, "E135", {"start": v(3.55, 2.12) * mm, "end": v(1.5, -0.95) * mm});
            skLineSegment(sketch, "E136", {"start": v(-1.5, -0.95) * mm, "end": v(-3.55, 2.12) * mm});
            skLineSegment(sketch, "E137", {"start": v(-7.45, 2.12) * mm, "end": v(-9.5, -0.95) * mm});
            skSolve(sketch);
        }
        {
            var Q1;
            Q1=makeQuery(id+"F2.imprint","IMPRINT",FACE,{"disambiguationData":[TD([[makeQuery(id+"F2.imprint","IMPRINT",EDGE,{"derivedFrom":sQuery(id+"F2.wireOp",EDGE,"E90.bottom")}),-1.0]])]});
            var Q2;
            Q2=makeQuery(id+"F1.imprint","IMPRINT",FACE,{"disambiguationData":[TD([[makeQuery(id+"F1.imprint","IMPRINT",EDGE,{"derivedFrom":sQuery(id+"F1.wireOp",EDGE,"E45.bottom")}),-1.0]])]});
            var Q3;
            Q3=sQuery(id+"F28.wireOp",EDGE,"E136");
            var Q4;
            Q4=sQuery(id+"F28.wireOp",EDGE,"E137");
            var Q5;
            Q5=sQuery(id+"F27.wireOp",EDGE,"E132");
            var Q6;
            Q6=sQuery(id+"F27.wireOp",EDGE,"E131");
            loft(context, id + "F29", {"operationType" : NewBodyOperationType.REMOVE, "addGuides" : true, "sheetProfilesArray" : [{ "sheetProfileEntities" : qUnion([Q1]) }, { "sheetProfileEntities" : qUnion([Q2]) }], "guidesArray" : [{ "guideEntities" : qUnion([Q3]), "guideDerivativeType" : LoftGuideDerivativeType.DEFAULT, "guideDerivativeMagnitude" : 1 }, { "guideEntities" : qUnion([Q4]), "guideDerivativeType" : LoftGuideDerivativeType.DEFAULT, "guideDerivativeMagnitude" : 1 }, { "guideEntities" : qUnion([Q5]), "guideDerivativeType" : LoftGuideDerivativeType.DEFAULT, "guideDerivativeMagnitude" : 1 }, { "guideEntities" : qUnion([Q6]), "guideDerivativeType" : LoftGuideDerivativeType.DEFAULT, "guideDerivativeMagnitude" : 1 }]});
        }
        {
            var Q1;
            Q1=makeQuery(id+"F2.imprint","IMPRINT",FACE,{"disambiguationData":[TD([[makeQuery(id+"F2.imprint","IMPRINT",EDGE,{"derivedFrom":sQuery(id+"F2.wireOp",EDGE,"E89.bottom")}),-1.0]])]});
            var Q2;
            Q2=makeQuery(id+"F1.imprint","IMPRINT",FACE,{"disambiguationData":[TD([[makeQuery(id+"F1.imprint","IMPRINT",EDGE,{"derivedFrom":sQuery(id+"F1.wireOp",EDGE,"E34.bottom")}),-1.0]])]});
            var Q3;
            Q3=sQuery(id+"F27.wireOp",EDGE,"E129");
            var Q4;
            Q4=sQuery(id+"F28.wireOp",EDGE,"E134");
            var Q5;
            Q5=sQuery(id+"F28.wireOp",EDGE,"E135");
            var Q6;
            Q6=sQuery(id+"F27.wireOp",EDGE,"E130");
            loft(context, id + "F30", {"operationType" : NewBodyOperationType.REMOVE, "addGuides" : true, "sheetProfilesArray" : [{ "sheetProfileEntities" : qUnion([Q1]) }, { "sheetProfileEntities" : qUnion([Q2]) }], "guidesArray" : [{ "guideEntities" : qUnion([Q3]), "guideDerivativeType" : LoftGuideDerivativeType.DEFAULT, "guideDerivativeMagnitude" : 1 }, { "guideEntities" : qUnion([Q4]), "guideDerivativeType" : LoftGuideDerivativeType.DEFAULT, "guideDerivativeMagnitude" : 1 }, { "guideEntities" : qUnion([Q5]), "guideDerivativeType" : LoftGuideDerivativeType.DEFAULT, "guideDerivativeMagnitude" : 1 }, { "guideEntities" : qUnion([Q6]), "guideDerivativeType" : LoftGuideDerivativeType.DEFAULT, "guideDerivativeMagnitude" : 1 }]});
        }
        {
            var Q0;
            Q0=makeQuery(id+"F1.imprint","IMPRINT",FACE,{"disambiguationData":[TD([[makeQuery(id+"F1.imprint","IMPRINT",EDGE,{"derivedFrom":sQuery(id+"F1.wireOp",EDGE,"E1.bottom")}),1.0]])]});
            var Q1;
            Q1=makeQuery(id+"F1.imprint","IMPRINT",FACE,{"disambiguationData":[TD([[makeQuery(id+"F1.imprint","IMPRINT",EDGE,{"derivedFrom":sQuery(id+"F1.wireOp",EDGE,"E45.bottom")}),-1.0]])]});
            var Q2;
            Q2=makeQuery(id+"F1.imprint","IMPRINT",FACE,{"disambiguationData":[TD([[makeQuery(id+"F1.imprint","IMPRINT",EDGE,{"derivedFrom":sQuery(id+"F1.wireOp",EDGE,"E1.bottom")}),-1.0]])]});
            var Q3;
            Q3=makeQuery(id+"F1.imprint","IMPRINT",FACE,{"disambiguationData":[TD([[makeQuery(id+"F1.imprint","IMPRINT",EDGE,{"derivedFrom":sQuery(id+"F1.wireOp",EDGE,"E67.bottom")}),-1.0]])]});
            var Q4;
            Q4=makeQuery(id+"F1.imprint","IMPRINT",FACE,{"disambiguationData":[TD([[makeQuery(id+"F1.imprint","IMPRINT",EDGE,{"derivedFrom":sQuery(id+"F1.wireOp",EDGE,"E56.bottom")}),-1.0]])]});
            var Q5;
            Q5=makeQuery(id+"F1.imprint","IMPRINT",FACE,{"disambiguationData":[TD([[makeQuery(id+"F1.imprint","IMPRINT",EDGE,{"derivedFrom":sQuery(id+"F1.wireOp",EDGE,"E34.bottom")}),-1.0]])]});
            var Q6;
            Q6=makeQuery(id+"F1.imprint","IMPRINT",FACE,{"disambiguationData":[TD([[makeQuery(id+"F1.imprint","IMPRINT",EDGE,{"derivedFrom":sQuery(id+"F1.wireOp",EDGE,"E12.bottom")}),-1.0]])]});
            var Q7;
            Q7=makeQuery(id+"F1.imprint","IMPRINT",FACE,{"disambiguationData":[TD([[makeQuery(id+"F1.imprint","IMPRINT",EDGE,{"derivedFrom":sQuery(id+"F1.wireOp",EDGE,"E23.bottom")}),-1.0]])]});
            extrude(context, id + "F31", {"entities" : qUnion([Q0, Q1, Q2, Q3, Q4, Q5, Q6, Q7]), "operationType" : NewBodyOperationType.ADD, "depth" : 0.2 * mm, "offsetDistance" : 25 * mm});
        }
        {
            var Q0;
            Q0=makeQuery(id+"F1.imprint","IMPRINT",FACE,{"disambiguationData":[TD([[makeQuery(id+"F1.imprint","IMPRINT",EDGE,{"derivedFrom":sQuery(id+"F1.wireOp",EDGE,"E0.bottom")}),-1.0]])]});
            extrude(context, id + "F32", {"entities" : qUnion([Q0]), "operationType" : NewBodyOperationType.ADD, "depth" : 7 * mm, "offsetDistance" : 25 * mm});
        }
        {
            var Q0;
            Q0=makeQuery(id+"F32.opExtrude","SWEPT_FACE",FACE,{"disambiguationData":[OSD([sQuery(id+"F1.wireOp",EDGE,"E0.right")])]});
            var sketch = newSketch(context, id + "F33", { "sketchPlane" : qUnion([Q0])});
            skPoint(sketch, "E138", {"position": v(-15, 5) * mm});
            skPoint(sketch, "E139", {"position": v(-10.5, 5) * mm});
            skPoint(sketch, "E140", {"position": v(-7.5, 5) * mm});
            skPoint(sketch, "E141", {"position": v(-4.5, 5) * mm});
            skPoint(sketch, "E142", {"position": v(-1.5, 5) * mm});
            skPoint(sketch, "E143", {"position": v(1.5, 5) * mm});
            skPoint(sketch, "E144", {"position": v(4.5, 5) * mm});
            skPoint(sketch, "E145", {"position": v(7.5, 5) * mm});
            skPoint(sketch, "E146", {"position": v(10.5, 5) * mm});
            skPoint(sketch, "E147", {"position": v(15, 5) * mm});
            skLineSegment(sketch, "E148", {"start": v(-15, 5) * mm, "end": v(-10.5, 5) * mm, "construction": true});
            skLineSegment(sketch, "E149", {"start": v(-10.5, 5) * mm, "end": v(-7.5, 5) * mm, "construction": true});
            skLineSegment(sketch, "E150", {"start": v(-7.5, 5) * mm, "end": v(-4.5, 5) * mm, "construction": true});
            skLineSegment(sketch, "E151", {"start": v(-4.5, 5) * mm, "end": v(-1.5, 5) * mm, "construction": true});
            skLineSegment(sketch, "E152", {"start": v(-1.5, 5) * mm, "end": v(1.5, 5) * mm, "construction": true});
            skLineSegment(sketch, "E153", {"start": v(1.5, 5) * mm, "end": v(4.5, 5) * mm, "construction": true});
            skLineSegment(sketch, "E154", {"start": v(4.5, 5) * mm, "end": v(7.5, 5) * mm, "construction": true});
            skLineSegment(sketch, "E155", {"start": v(7.5, 5) * mm, "end": v(10.5, 5) * mm, "construction": true});
            skLineSegment(sketch, "E156", {"start": v(10.5, 5) * mm, "end": v(15, 5) * mm, "construction": true});
            skCircle(sketch, "E157", {"center": v(-10.5, 5) * mm, "radius": 0.75 * mm});
            skCircle(sketch, "E158", {"center": v(-7.5, 5) * mm, "radius": 0.75 * mm});
            skCircle(sketch, "E159", {"center": v(-4.5, 5) * mm, "radius": 0.75 * mm});
            skCircle(sketch, "E160", {"center": v(-1.5, 5) * mm, "radius": 0.75 * mm});
            skCircle(sketch, "E161", {"center": v(1.5, 5) * mm, "radius": 0.75 * mm});
            skCircle(sketch, "E162", {"center": v(4.5, 5) * mm, "radius": 0.75 * mm});
            skCircle(sketch, "E163", {"center": v(7.5, 5) * mm, "radius": 0.75 * mm});
            skCircle(sketch, "E164", {"center": v(10.5, 5) * mm, "radius": 0.75 * mm});
            skSolve(sketch);
        }
        {
            var Q0;
            Q0=makeQuery(id+"F33.imprint","IMPRINT",FACE,{"disambiguationData":[TD([[makeQuery(id+"F33.imprint","IMPRINT",EDGE,{"derivedFrom":sQuery(id+"F33.wireOp",EDGE,"E157")}),1.0]])]});
            var Q1;
            Q1=makeQuery(id+"F33.imprint","IMPRINT",FACE,{"disambiguationData":[TD([[makeQuery(id+"F33.imprint","IMPRINT",EDGE,{"derivedFrom":sQuery(id+"F33.wireOp",EDGE,"E158")}),1.0]])]});
            var Q2;
            Q2=makeQuery(id+"F33.imprint","IMPRINT",FACE,{"disambiguationData":[TD([[makeQuery(id+"F33.imprint","IMPRINT",EDGE,{"derivedFrom":sQuery(id+"F33.wireOp",EDGE,"E159")}),1.0]])]});
            var Q3;
            Q3=makeQuery(id+"F33.imprint","IMPRINT",FACE,{"disambiguationData":[TD([[makeQuery(id+"F33.imprint","IMPRINT",EDGE,{"derivedFrom":sQuery(id+"F33.wireOp",EDGE,"E160")}),1.0]])]});
            var Q4;
            Q4=makeQuery(id+"F33.imprint","IMPRINT",FACE,{"disambiguationData":[TD([[makeQuery(id+"F33.imprint","IMPRINT",EDGE,{"derivedFrom":sQuery(id+"F33.wireOp",EDGE,"E161")}),1.0]])]});
            var Q5;
            Q5=makeQuery(id+"F33.imprint","IMPRINT",FACE,{"disambiguationData":[TD([[makeQuery(id+"F33.imprint","IMPRINT",EDGE,{"derivedFrom":sQuery(id+"F33.wireOp",EDGE,"E162")}),1.0]])]});
            var Q6;
            Q6=makeQuery(id+"F33.imprint","IMPRINT",FACE,{"disambiguationData":[TD([[makeQuery(id+"F33.imprint","IMPRINT",EDGE,{"derivedFrom":sQuery(id+"F33.wireOp",EDGE,"E163")}),1.0]])]});
            var Q7;
            Q7=makeQuery(id+"F33.imprint","IMPRINT",FACE,{"disambiguationData":[TD([[makeQuery(id+"F33.imprint","IMPRINT",EDGE,{"derivedFrom":sQuery(id+"F33.wireOp",EDGE,"E164")}),1.0]])]});
            extrude(context, id + "F34", {"entities" : qUnion([Q0, Q1, Q2, Q3, Q4, Q5, Q6, Q7]), "operationType" : NewBodyOperationType.REMOVE, "endBound" : BoundingType.UP_TO_NEXT, "oppositeDirection" : true, "depth" : 25 * mm, "offsetDistance" : 25 * mm});
        }
        {
            var Q0;
            Q0=makeQuery(id+"F32.opExtrude","SWEPT_FACE",FACE,{"disambiguationData":[OSD([sQuery(id+"F1.wireOp",EDGE,"E0.right")])]});
            var sketch = newSketch(context, id + "F35", { "sketchPlane" : qUnion([Q0])});
            skText(sketch, "E165", { "text": "G 7 6 5 4 3 2 1", "fontName": "OpenSans-Bold.ttf"});
            skPoint(sketch, "E166", {"position": v(-11.5, 3.5) * mm});
            const initialGuessF35  = {"E165": [-0.0115, 0.00093, 1, 0, 0.00257]};
            skSetInitialGuess(sketch, initialGuessF35);
            skSolve(sketch);
        }
        {
            var Q0;
            Q0 = qSketchRegion(id + "F35", true);
            extrude(context, id + "F36", {"entities" : qUnion([Q0]), "operationType" : NewBodyOperationType.REMOVE, "oppositeDirection" : true, "depth" : 0.5 * mm, "offsetDistance" : 25 * mm});
        }
        {
            var Q0;
            Q0=qCreatedBy(makeId("Right.planeOp"),FACE);
            var sketch = newSketch(context, id + "F37", { "sketchPlane" : qUnion([Q0])});
            skLineSegment(sketch, "E167", {"start": v(0, 0) * mm, "end": v(0, 40) * mm, "construction": true});
            skSolve(sketch);
        }
        {
            var Q0;
            Q0=makeQuery(id+"F3.opExtrude","SWEPT_BODY",BODY,{"disambiguationData":[OSD([sQuery(id+"F1.wireOp",EDGE,"E86.0"),sQuery(id+"F1.wireOp",EDGE,"E86.1"),sQuery(id+"F1.wireOp",EDGE,"E86.2"),sQuery(id+"F1.wireOp",EDGE,"E86.3")])]});
            var Q1;
            Q1=sQuery(id+"F37.wireOp",EDGE,"E167");
            transform(context, id + "F38", {"entities" : qUnion([Q0]), "transformType" : TransformType.ROTATION, "transformAxis" : qUnion([Q1]), "angle" : 180 * degree, "makeCopy" : false});
        }
        {
            var Q0;
            Q0=makeQuery(id+"F3.opExtrude","CAP_FACE",FACE,{"disambiguationData":[OSD([sQuery(id+"F1.wireOp",EDGE,"E86.0"),sQuery(id+"F1.wireOp",EDGE,"E86.1"),sQuery(id+"F1.wireOp",EDGE,"E86.2"),sQuery(id+"F1.wireOp",EDGE,"E86.3")])],"isStart":false});
            var sketch = newSketch(context, id + "F39", { "sketchPlane" : qUnion([Q0])});
            skLineSegment(sketch, "E168.bottom", {"start": v(-9, 14) * mm, "end": v(-8, 14) * mm});
            skLineSegment(sketch, "E168.top", {"start": v(-9, 13) * mm, "end": v(-8, 13) * mm});
            skLineSegment(sketch, "E168.left", {"start": v(-9, 14) * mm, "end": v(-9, 13) * mm});
            skLineSegment(sketch, "E168.right", {"start": v(-8, 14) * mm, "end": v(-8, 13) * mm});
            skLineSegment(sketch, "E169.bottom", {"start": v(8, 14) * mm, "end": v(9, 14) * mm});
            skLineSegment(sketch, "E169.top", {"start": v(8, 13) * mm, "end": v(9, 13) * mm});
            skLineSegment(sketch, "E169.left", {"start": v(8, 14) * mm, "end": v(8, 13) * mm});
            skLineSegment(sketch, "E169.right", {"start": v(9, 14) * mm, "end": v(9, 13) * mm});
            skLineSegment(sketch, "E170.bottom", {"start": v(8, -13) * mm, "end": v(9, -13) * mm});
            skLineSegment(sketch, "E170.top", {"start": v(8, -14) * mm, "end": v(9, -14) * mm});
            skLineSegment(sketch, "E170.left", {"start": v(8, -13) * mm, "end": v(8, -14) * mm});
            skLineSegment(sketch, "E170.right", {"start": v(9, -13) * mm, "end": v(9, -14) * mm});
            skLineSegment(sketch, "E171.bottom", {"start": v(-9, -13) * mm, "end": v(-8, -13) * mm});
            skLineSegment(sketch, "E171.top", {"start": v(-9, -14) * mm, "end": v(-8, -14) * mm});
            skLineSegment(sketch, "E171.left", {"start": v(-9, -13) * mm, "end": v(-9, -14) * mm});
            skLineSegment(sketch, "E171.right", {"start": v(-8, -13) * mm, "end": v(-8, -14) * mm});
            skSolve(sketch);
        }
        {
            var Q0;
            Q0=makeQuery(id+"F39.imprint","IMPRINT",FACE,{"disambiguationData":[TD([[makeQuery(id+"F39.imprint","IMPRINT",EDGE,{"derivedFrom":sQuery(id+"F39.wireOp",EDGE,"E168.bottom")}),-1.0]])]});
            var Q1;
            Q1=makeQuery(id+"F39.imprint","IMPRINT",FACE,{"disambiguationData":[TD([[makeQuery(id+"F39.imprint","IMPRINT",EDGE,{"derivedFrom":sQuery(id+"F39.wireOp",EDGE,"E169.bottom")}),-1.0]])]});
            var Q2;
            Q2=makeQuery(id+"F39.imprint","IMPRINT",FACE,{"disambiguationData":[TD([[makeQuery(id+"F39.imprint","IMPRINT",EDGE,{"derivedFrom":sQuery(id+"F39.wireOp",EDGE,"E171.bottom")}),-1.0]])]});
            var Q3;
            Q3=makeQuery(id+"F39.imprint","IMPRINT",FACE,{"disambiguationData":[TD([[makeQuery(id+"F39.imprint","IMPRINT",EDGE,{"derivedFrom":sQuery(id+"F39.wireOp",EDGE,"E170.bottom")}),-1.0]])]});
            extrude(context, id + "F40", {"entities" : qUnion([Q0, Q1, Q2, Q3]), "operationType" : NewBodyOperationType.ADD, "depth" : 2.6 * mm, "offsetDistance" : 25 * mm});
        }
    });
